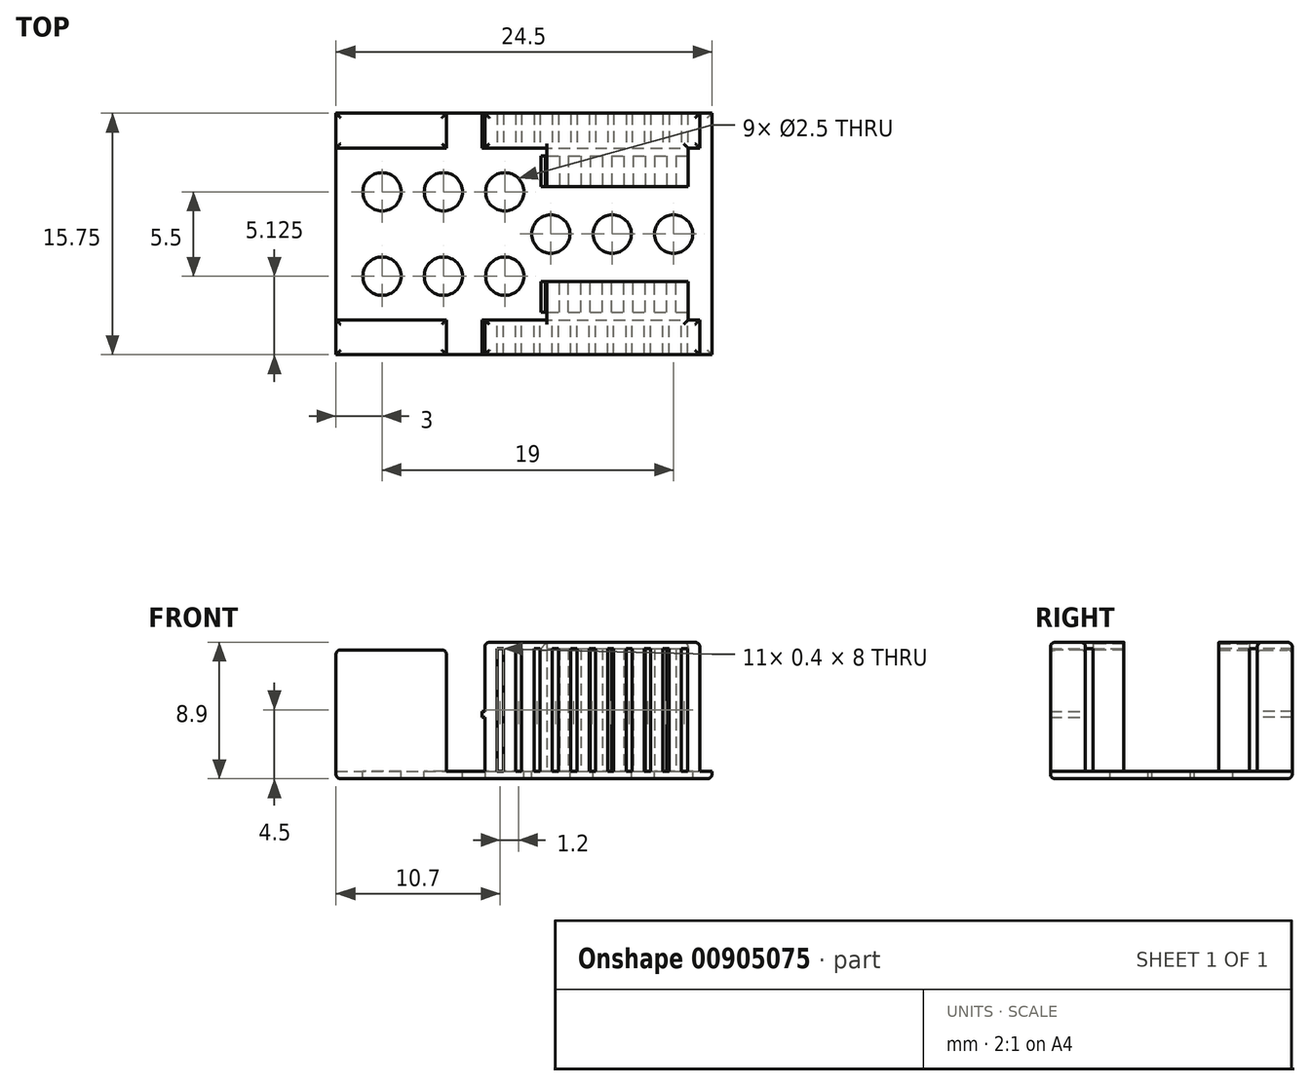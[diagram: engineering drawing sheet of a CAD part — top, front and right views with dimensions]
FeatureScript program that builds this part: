
annotation { "Feature Type Name" : "Feature", "Feature Type Description" : "" }
export const myFeature = defineFeature(function(context is Context, id is Id, definition is map)
    precondition{}
    {
        {
            var Q0;
            Q0=qCreatedBy(makeId("Top.planeOp"),FACE);
            var sketch = newSketch(context, id + "F0", { "sketchPlane" : qUnion([Q0])});
            skLineSegment(sketch, "E0.bottom", {"start": v(0, 0) * mm, "end": v(24.5, 0) * mm});
            skLineSegment(sketch, "E0.top", {"start": v(0, -15.75) * mm, "end": v(24.5, -15.75) * mm});
            skLineSegment(sketch, "E0.left", {"start": v(0, 0) * mm, "end": v(0, -15.75) * mm});
            skLineSegment(sketch, "E0.right", {"start": v(24.5, 0) * mm, "end": v(24.5, -15.75) * mm});
            skSolve(sketch);
        }
        {
            var Q0;
            Q0 = qSketchRegion(id + "F0", true);
            extrude(context, id + "F1", {"entities" : qUnion([Q0]), "depth" : .5 * mm, "offsetDistance" : 25 * mm});
        }
        {
            var Q0;
            Q0=makeQuery(id+"F1.opExtrude","CAP_FACE",FACE,{"disambiguationData":[OSD([sQuery(id+"F0.wireOp",EDGE,"E0.bottom"),sQuery(id+"F0.wireOp",EDGE,"E0.top"),sQuery(id+"F0.wireOp",EDGE,"E0.left"),sQuery(id+"F0.wireOp",EDGE,"E0.right")])],"isStart":false});
            var sketch = newSketch(context, id + "F2", { "sketchPlane" : qUnion([Q0])});
            skLineSegment(sketch, "E1", {"start": v(0, -2.28) * mm, "end": v(24.5, -2.27) * mm, "construction": true});
            skPoint(sketch, "E2", {"position": v(0, -7.87) * mm});
            skLineSegment(sketch, "E3", {"start": v(0, -7.87) * mm, "end": v(24.5, -7.87) * mm, "construction": true});
            skLineSegment(sketch, "E4.bottom", {"start": v(0, -2.28) * mm, "end": v(7.2, -2.28) * mm});
            skLineSegment(sketch, "E4.top", {"start": v(0, 0) * mm, "end": v(7.2, 0) * mm});
            skLineSegment(sketch, "E4.left", {"start": v(0, -2.28) * mm, "end": v(0, 0) * mm});
            skLineSegment(sketch, "E4.right", {"start": v(7.2, -2.28) * mm, "end": v(7.2, 0) * mm});
            skLineSegment(sketch, "E5.MirrorCS", {"start": v(0, -15.75) * mm, "end": v(7.2, -15.75) * mm});
            skLineSegment(sketch, "E6.MirrorCS", {"start": v(7.2, -13.47) * mm, "end": v(7.2, -15.75) * mm});
            skLineSegment(sketch, "E7.MirrorCS", {"start": v(0, -13.47) * mm, "end": v(0, -15.75) * mm});
            skLineSegment(sketch, "E8.MirrorCS", {"start": v(0, -13.47) * mm, "end": v(7.2, -13.47) * mm});
            skSolve(sketch);
        }
        {
            var Q0;
            Q0 = qSketchRegion(id + "F2", true);
            extrude(context, id + "F3", {"entities" : qUnion([Q0]), "operationType" : NewBodyOperationType.ADD, "depth" : 7.9 * mm, "offsetDistance" : 25 * mm});
        }
        {
            var Q0;
            Q0=makeQuery(id+"F1.opExtrude","CAP_FACE",FACE,{"disambiguationData":[OSD([sQuery(id+"F0.wireOp",EDGE,"E0.bottom"),sQuery(id+"F0.wireOp",EDGE,"E0.top"),sQuery(id+"F0.wireOp",EDGE,"E0.left"),sQuery(id+"F0.wireOp",EDGE,"E0.right")])],"isStart":false});
            var sketch = newSketch(context, id + "F4", { "sketchPlane" : qUnion([Q0])});
            skLineSegment(sketch, "E9", {"start": v(0, -7.88) * mm, "end": v(24.5, -7.87) * mm, "construction": true});
            skLineSegment(sketch, "E10.bottom", {"start": v(9.7, 0) * mm, "end": v(10.5, 0) * mm});
            skLineSegment(sketch, "E10.top", {"start": v(9.7, -2.28) * mm, "end": v(10.5, -2.28) * mm});
            skLineSegment(sketch, "E10.left", {"start": v(9.7, 0) * mm, "end": v(9.7, -2.28) * mm});
            skLineSegment(sketch, "E10.right", {"start": v(10.5, 0) * mm, "end": v(10.5, -2.28) * mm});
            skLineSegment(sketch, "E11.1.0.0", {"start": v(10.9, 0) * mm, "end": v(10.9, -2.28) * mm});
            skLineSegment(sketch, "E11.1.0.1", {"start": v(10.9, 0) * mm, "end": v(11.7, 0) * mm});
            skLineSegment(sketch, "E11.1.0.2", {"start": v(11.7, 0) * mm, "end": v(11.7, -2.28) * mm});
            skLineSegment(sketch, "E11.1.0.3", {"start": v(10.9, -2.28) * mm, "end": v(11.7, -2.28) * mm});
            skLineSegment(sketch, "E11.2.0.0", {"start": v(12.1, 0) * mm, "end": v(12.1, -2.28) * mm});
            skLineSegment(sketch, "E11.2.0.1", {"start": v(12.1, 0) * mm, "end": v(12.9, 0) * mm});
            skLineSegment(sketch, "E11.2.0.2", {"start": v(12.9, 0) * mm, "end": v(12.9, -2.28) * mm});
            skLineSegment(sketch, "E11.2.0.3", {"start": v(12.1, -2.28) * mm, "end": v(12.9, -2.28) * mm});
            skLineSegment(sketch, "E11.3.0.0", {"start": v(13.3, 0) * mm, "end": v(13.3, -2.28) * mm});
            skLineSegment(sketch, "E11.3.0.1", {"start": v(13.3, 0) * mm, "end": v(14.1, 0) * mm});
            skLineSegment(sketch, "E11.3.0.2", {"start": v(14.1, 0) * mm, "end": v(14.1, -2.28) * mm});
            skLineSegment(sketch, "E11.3.0.3", {"start": v(13.3, -2.28) * mm, "end": v(14.1, -2.28) * mm});
            skLineSegment(sketch, "E11.4.0.0", {"start": v(14.5, 0) * mm, "end": v(14.5, -2.28) * mm});
            skLineSegment(sketch, "E11.4.0.1", {"start": v(14.5, 0) * mm, "end": v(15.3, 0) * mm});
            skLineSegment(sketch, "E11.4.0.2", {"start": v(15.3, 0) * mm, "end": v(15.3, -2.28) * mm});
            skLineSegment(sketch, "E11.4.0.3", {"start": v(14.5, -2.28) * mm, "end": v(15.3, -2.28) * mm});
            skLineSegment(sketch, "E11.direction1", {"start": v(9.7, -2.28) * mm, "end": v(10.9, -2.28) * mm, "construction": true});
            skLineSegment(sketch, "E12.MirrorCS", {"start": v(9.7, -13.48) * mm, "end": v(10.5, -13.48) * mm});
            skLineSegment(sketch, "E13.MirrorCS", {"start": v(10.9, -15.75) * mm, "end": v(11.7, -15.75) * mm});
            skLineSegment(sketch, "E14.MirrorCS", {"start": v(14.5, -15.75) * mm, "end": v(14.5, -13.48) * mm});
            skLineSegment(sketch, "E15.MirrorCS", {"start": v(14.5, -15.75) * mm, "end": v(15.3, -15.75) * mm});
            skLineSegment(sketch, "E16.MirrorCS", {"start": v(12.1, -13.48) * mm, "end": v(12.9, -13.48) * mm});
            skLineSegment(sketch, "E17.MirrorCS", {"start": v(15.3, -15.75) * mm, "end": v(15.3, -13.48) * mm});
            skLineSegment(sketch, "E18.MirrorCS", {"start": v(10.9, -15.75) * mm, "end": v(10.9, -13.48) * mm});
            skLineSegment(sketch, "E19.MirrorCS", {"start": v(12.9, -15.75) * mm, "end": v(12.9, -13.48) * mm});
            skLineSegment(sketch, "E20.MirrorCS", {"start": v(13.3, -15.75) * mm, "end": v(14.1, -15.75) * mm});
            skLineSegment(sketch, "E21.MirrorCS", {"start": v(14.5, -13.48) * mm, "end": v(15.3, -13.48) * mm});
            skLineSegment(sketch, "E22.MirrorCS", {"start": v(10.5, -15.75) * mm, "end": v(10.5, -13.48) * mm});
            skLineSegment(sketch, "E23.MirrorCS", {"start": v(12.1, -15.75) * mm, "end": v(12.9, -15.75) * mm});
            skLineSegment(sketch, "E24.MirrorCS", {"start": v(9.7, -13.48) * mm, "end": v(10.9, -13.48) * mm, "construction": true});
            skLineSegment(sketch, "E25.MirrorCS", {"start": v(13.3, -15.75) * mm, "end": v(13.3, -13.48) * mm});
            skLineSegment(sketch, "E26.MirrorCS", {"start": v(9.7, -15.75) * mm, "end": v(9.7, -13.48) * mm});
            skLineSegment(sketch, "E27.MirrorCS", {"start": v(12.1, -15.75) * mm, "end": v(12.1, -13.48) * mm});
            skLineSegment(sketch, "E28.MirrorCS", {"start": v(14.1, -15.75) * mm, "end": v(14.1, -13.48) * mm});
            skLineSegment(sketch, "E29.MirrorCS", {"start": v(13.3, -13.48) * mm, "end": v(14.1, -13.48) * mm});
            skLineSegment(sketch, "E30.MirrorCS", {"start": v(9.7, -15.75) * mm, "end": v(10.5, -15.75) * mm});
            skLineSegment(sketch, "E31.MirrorCS", {"start": v(10.9, -13.48) * mm, "end": v(11.7, -13.48) * mm});
            skLineSegment(sketch, "E32.MirrorCS", {"start": v(11.7, -15.75) * mm, "end": v(11.7, -13.48) * mm});
            skLineSegment(sketch, "E33.0.5.0", {"start": v(15.7, 0) * mm, "end": v(15.7, -2.28) * mm});
            skLineSegment(sketch, "E33.3.5.0", {"start": v(15.7, 0) * mm, "end": v(16.5, 0) * mm});
            skLineSegment(sketch, "E33.6.5.0", {"start": v(16.5, 0) * mm, "end": v(16.5, -2.28) * mm});
            skLineSegment(sketch, "E33.9.5.0", {"start": v(15.7, -2.28) * mm, "end": v(16.5, -2.28) * mm});
            skLineSegment(sketch, "E33.0.6.0", {"start": v(16.9, 0) * mm, "end": v(16.9, -2.28) * mm});
            skLineSegment(sketch, "E33.3.6.0", {"start": v(16.9, 0) * mm, "end": v(17.7, 0) * mm});
            skLineSegment(sketch, "E33.6.6.0", {"start": v(17.7, 0) * mm, "end": v(17.7, -2.28) * mm});
            skLineSegment(sketch, "E33.9.6.0", {"start": v(16.9, -2.28) * mm, "end": v(17.7, -2.28) * mm});
            skLineSegment(sketch, "E33.0.7.0", {"start": v(18.1, 0) * mm, "end": v(18.1, -2.28) * mm});
            skLineSegment(sketch, "E33.3.7.0", {"start": v(18.1, 0) * mm, "end": v(18.9, 0) * mm});
            skLineSegment(sketch, "E33.6.7.0", {"start": v(18.9, 0) * mm, "end": v(18.9, -2.28) * mm});
            skLineSegment(sketch, "E33.9.7.0", {"start": v(18.1, -2.28) * mm, "end": v(18.9, -2.28) * mm});
            skLineSegment(sketch, "E34.MirrorCS", {"start": v(18.9, -15.75) * mm, "end": v(18.9, -13.47) * mm});
            skLineSegment(sketch, "E35.MirrorCS", {"start": v(16.5, -15.75) * mm, "end": v(16.5, -13.48) * mm});
            skLineSegment(sketch, "E36.MirrorCS", {"start": v(15.7, -13.48) * mm, "end": v(16.5, -13.48) * mm});
            skLineSegment(sketch, "E37.MirrorCS", {"start": v(15.7, -15.75) * mm, "end": v(15.7, -13.48) * mm});
            skLineSegment(sketch, "E38.MirrorCS", {"start": v(16.9, -15.75) * mm, "end": v(16.9, -13.48) * mm});
            skLineSegment(sketch, "E39.MirrorCS", {"start": v(18.1, -15.75) * mm, "end": v(18.1, -13.47) * mm});
            skLineSegment(sketch, "E40.MirrorCS", {"start": v(18.1, -15.75) * mm, "end": v(18.9, -15.75) * mm});
            skLineSegment(sketch, "E41.MirrorCS", {"start": v(15.7, -15.75) * mm, "end": v(16.5, -15.75) * mm});
            skLineSegment(sketch, "E42.MirrorCS", {"start": v(17.7, -15.75) * mm, "end": v(17.7, -13.48) * mm});
            skLineSegment(sketch, "E43.MirrorCS", {"start": v(16.9, -15.75) * mm, "end": v(17.7, -15.75) * mm});
            skLineSegment(sketch, "E44.MirrorCS", {"start": v(16.9, -13.48) * mm, "end": v(17.7, -13.48) * mm});
            skLineSegment(sketch, "E45.MirrorCS", {"start": v(18.1, -13.47) * mm, "end": v(18.9, -13.47) * mm});
            skLineSegment(sketch, "E46.0.8.0", {"start": v(19.3, 0) * mm, "end": v(19.3, -2.28) * mm});
            skLineSegment(sketch, "E46.3.8.0", {"start": v(19.3, 0) * mm, "end": v(20.1, 0) * mm});
            skLineSegment(sketch, "E46.6.8.0", {"start": v(20.1, 0) * mm, "end": v(20.1, -2.28) * mm});
            skLineSegment(sketch, "E46.9.8.0", {"start": v(19.3, -2.28) * mm, "end": v(20.1, -2.28) * mm});
            skLineSegment(sketch, "E46.0.9.0", {"start": v(20.5, 0) * mm, "end": v(20.5, -2.28) * mm});
            skLineSegment(sketch, "E46.3.9.0", {"start": v(20.5, 0) * mm, "end": v(21.3, 0) * mm});
            skLineSegment(sketch, "E46.6.9.0", {"start": v(21.3, 0) * mm, "end": v(21.3, -2.28) * mm});
            skLineSegment(sketch, "E46.9.9.0", {"start": v(20.5, -2.28) * mm, "end": v(21.3, -2.28) * mm});
            skLineSegment(sketch, "E46.0.10.0", {"start": v(21.7, 0) * mm, "end": v(21.7, -2.28) * mm});
            skLineSegment(sketch, "E46.3.10.0", {"start": v(21.7, 0) * mm, "end": v(22.5, 0) * mm});
            skLineSegment(sketch, "E46.6.10.0", {"start": v(22.5, 0) * mm, "end": v(22.5, -2.28) * mm});
            skLineSegment(sketch, "E46.9.10.0", {"start": v(21.7, -2.28) * mm, "end": v(22.5, -2.28) * mm});
            skLineSegment(sketch, "E46.0.11.0", {"start": v(22.9, 0) * mm, "end": v(22.9, -2.28) * mm});
            skLineSegment(sketch, "E46.3.11.0", {"start": v(22.9, 0) * mm, "end": v(23.7, 0) * mm});
            skLineSegment(sketch, "E46.6.11.0", {"start": v(23.7, 0) * mm, "end": v(23.7, -2.28) * mm});
            skLineSegment(sketch, "E46.9.11.0", {"start": v(22.9, -2.28) * mm, "end": v(23.7, -2.28) * mm});
            skLineSegment(sketch, "E47.MirrorCS", {"start": v(19.3, -13.47) * mm, "end": v(20.1, -13.47) * mm});
            skLineSegment(sketch, "E48.MirrorCS", {"start": v(19.3, -15.75) * mm, "end": v(19.3, -13.47) * mm});
            skLineSegment(sketch, "E49.MirrorCS", {"start": v(20.1, -15.75) * mm, "end": v(20.1, -13.47) * mm});
            skLineSegment(sketch, "E50.MirrorCS", {"start": v(19.3, -15.75) * mm, "end": v(20.1, -15.75) * mm});
            skLineSegment(sketch, "E51.MirrorCS", {"start": v(20.5, -15.75) * mm, "end": v(20.5, -13.47) * mm});
            skLineSegment(sketch, "E52.MirrorCS", {"start": v(20.5, -13.47) * mm, "end": v(21.3, -13.47) * mm});
            skLineSegment(sketch, "E53.MirrorCS", {"start": v(21.3, -15.75) * mm, "end": v(21.3, -13.47) * mm});
            skLineSegment(sketch, "E54.MirrorCS", {"start": v(20.5, -15.75) * mm, "end": v(21.3, -15.75) * mm});
            skLineSegment(sketch, "E55.MirrorCS", {"start": v(21.7, -15.75) * mm, "end": v(21.7, -13.47) * mm});
            skLineSegment(sketch, "E56.MirrorCS", {"start": v(21.7, -13.47) * mm, "end": v(22.5, -13.47) * mm});
            skLineSegment(sketch, "E57.MirrorCS", {"start": v(22.5, -15.75) * mm, "end": v(22.5, -13.47) * mm});
            skLineSegment(sketch, "E58.MirrorCS", {"start": v(21.7, -15.75) * mm, "end": v(22.5, -15.75) * mm});
            skLineSegment(sketch, "E59.MirrorCS", {"start": v(22.9, -15.75) * mm, "end": v(22.9, -13.47) * mm});
            skLineSegment(sketch, "E60.MirrorCS", {"start": v(22.9, -13.47) * mm, "end": v(23.7, -13.47) * mm});
            skLineSegment(sketch, "E61.MirrorCS", {"start": v(23.7, -15.75) * mm, "end": v(23.7, -13.47) * mm});
            skLineSegment(sketch, "E62.MirrorCS", {"start": v(22.9, -15.75) * mm, "end": v(23.7, -15.75) * mm});
            skSolve(sketch);
        }
        {
            var Q0;
            Q0 = qSketchRegion(id + "F4", true);
            extrude(context, id + "F5", {"entities" : qUnion([Q0]), "operationType" : NewBodyOperationType.ADD, "depth" : 8 * mm, "offsetDistance" : 25 * mm});
        }
        {
            var Q0;
            Q0=makeQuery(id+"F5.opExtrude","SWEPT_FACE",FACE,{"disambiguationData":[OSD([sQuery(id+"F4.wireOp",EDGE,"E10.left")])]});
            var sketch = newSketch(context, id + "F6", { "sketchPlane" : qUnion([Q0])});
            skLineSegment(sketch, "E63.bottom", {"start": v(0, 4) * mm, "end": v(2.27, 4) * mm});
            skLineSegment(sketch, "E63.top", {"start": v(0, 4.4) * mm, "end": v(2.28, 4.4) * mm});
            skLineSegment(sketch, "E63.left", {"start": v(0, 4) * mm, "end": v(0, 4.4) * mm});
            skLineSegment(sketch, "E63.right", {"start": v(2.28, 4) * mm, "end": v(2.28, 4.4) * mm});
            skLineSegment(sketch, "E64", {"start": v(7.88, 0) * mm, "end": v(7.88, 8.23) * mm, "construction": true});
            skLineSegment(sketch, "E65.MirrorCS", {"start": v(15.75, 4) * mm, "end": v(15.75, 4.4) * mm});
            skLineSegment(sketch, "E66.MirrorCS", {"start": v(13.47, 4) * mm, "end": v(13.47, 4.4) * mm});
            skLineSegment(sketch, "E67.MirrorCS", {"start": v(15.75, 4) * mm, "end": v(13.48, 4) * mm});
            skLineSegment(sketch, "E68.MirrorCS", {"start": v(15.75, 4.4) * mm, "end": v(13.47, 4.4) * mm});
            skSolve(sketch);
        }
        {
            var Q0;
            Q0 = qSketchRegion(id + "F6", true);
            extrude(context, id + "F7", {"entities" : qUnion([Q0]), "operationType" : NewBodyOperationType.ADD, "depth" : .2 * mm, "offsetDistance" : 25 * mm});
        }
        {
            var Q0;
            Q0=makeQuery(id+"F1.opExtrude","CAP_FACE",FACE,{"disambiguationData":[OSD([sQuery(id+"F0.wireOp",EDGE,"E0.bottom"),sQuery(id+"F0.wireOp",EDGE,"E0.top"),sQuery(id+"F0.wireOp",EDGE,"E0.left"),sQuery(id+"F0.wireOp",EDGE,"E0.right")])],"isStart":false});
            var sketch = newSketch(context, id + "F8", { "sketchPlane" : qUnion([Q0])});
            skLineSegment(sketch, "E69", {"start": v(13.75, 0) * mm, "end": v(13.75, -15.77) * mm, "construction": true});
            skLineSegment(sketch, "E70", {"start": v(24.5, -7.88) * mm, "end": v(0, -7.88) * mm, "construction": true});
            skLineSegment(sketch, "E71.bottom", {"start": v(13.75, -2.78) * mm, "end": v(14.55, -2.78) * mm});
            skLineSegment(sketch, "E71.top", {"start": v(13.75, -4.78) * mm, "end": v(14.55, -4.78) * mm});
            skLineSegment(sketch, "E71.left", {"start": v(13.75, -2.78) * mm, "end": v(13.75, -4.78) * mm});
            skLineSegment(sketch, "E71.right", {"start": v(14.55, -2.78) * mm, "end": v(14.55, -4.78) * mm});
            skLineSegment(sketch, "E72.direction1", {"start": v(13.75, -4.78) * mm, "end": v(15.15, -4.78) * mm, "construction": true});
            skLineSegment(sketch, "E72.direction2", {"start": v(13.75, -4.78) * mm, "end": v(13.75, -7.28) * mm, "construction": true});
            skLineSegment(sketch, "E73.0.1.0", {"start": v(15.15, -2.78) * mm, "end": v(15.15, -4.78) * mm});
            skLineSegment(sketch, "E73.3.1.0", {"start": v(15.15, -2.78) * mm, "end": v(15.95, -2.78) * mm});
            skLineSegment(sketch, "E73.6.1.0", {"start": v(15.15, -4.78) * mm, "end": v(15.95, -4.78) * mm});
            skLineSegment(sketch, "E73.9.1.0", {"start": v(15.95, -2.78) * mm, "end": v(15.95, -4.78) * mm});
            skLineSegment(sketch, "E74.MirrorCS", {"start": v(13.75, -10.98) * mm, "end": v(14.55, -10.98) * mm});
            skLineSegment(sketch, "E75.MirrorCS", {"start": v(15.15, -10.98) * mm, "end": v(15.95, -10.97) * mm});
            skLineSegment(sketch, "E76.MirrorCS", {"start": v(13.75, -12.98) * mm, "end": v(13.75, -10.98) * mm});
            skLineSegment(sketch, "E77.MirrorCS", {"start": v(14.55, -12.98) * mm, "end": v(14.55, -10.98) * mm});
            skLineSegment(sketch, "E78.MirrorCS", {"start": v(13.75, -12.98) * mm, "end": v(14.55, -12.98) * mm});
            skLineSegment(sketch, "E79.MirrorCS", {"start": v(15.15, -12.98) * mm, "end": v(15.95, -12.98) * mm});
            skLineSegment(sketch, "E80.MirrorCS", {"start": v(15.95, -12.97) * mm, "end": v(15.95, -10.98) * mm});
            skLineSegment(sketch, "E81.MirrorCS", {"start": v(15.15, -12.97) * mm, "end": v(15.15, -10.98) * mm});
            skLineSegment(sketch, "E82.MirrorCS", {"start": v(13.75, -10.98) * mm, "end": v(15.15, -10.98) * mm, "construction": true});
            skLineSegment(sketch, "E83.MirrorCS", {"start": v(13.75, -10.98) * mm, "end": v(13.75, -8.48) * mm, "construction": true});
            skLineSegment(sketch, "E84.0.2.0", {"start": v(16.55, -2.78) * mm, "end": v(16.55, -4.78) * mm});
            skLineSegment(sketch, "E84.3.2.0", {"start": v(16.55, -2.78) * mm, "end": v(17.35, -2.78) * mm});
            skLineSegment(sketch, "E84.6.2.0", {"start": v(16.55, -4.78) * mm, "end": v(17.35, -4.78) * mm});
            skLineSegment(sketch, "E84.9.2.0", {"start": v(17.35, -2.78) * mm, "end": v(17.35, -4.78) * mm});
            skLineSegment(sketch, "E85.MirrorCS", {"start": v(16.55, -10.98) * mm, "end": v(17.35, -10.98) * mm});
            skLineSegment(sketch, "E86.MirrorCS", {"start": v(16.55, -12.97) * mm, "end": v(17.35, -12.97) * mm});
            skLineSegment(sketch, "E87.MirrorCS", {"start": v(17.35, -12.97) * mm, "end": v(17.35, -10.98) * mm});
            skLineSegment(sketch, "E88.MirrorCS", {"start": v(16.55, -12.97) * mm, "end": v(16.55, -10.98) * mm});
            skLineSegment(sketch, "E89.0.3.0", {"start": v(17.95, -2.78) * mm, "end": v(17.95, -4.78) * mm});
            skLineSegment(sketch, "E89.3.3.0", {"start": v(17.95, -2.78) * mm, "end": v(18.75, -2.78) * mm});
            skLineSegment(sketch, "E89.6.3.0", {"start": v(17.95, -4.78) * mm, "end": v(18.75, -4.78) * mm});
            skLineSegment(sketch, "E89.9.3.0", {"start": v(18.75, -2.78) * mm, "end": v(18.75, -4.78) * mm});
            skLineSegment(sketch, "E89.0.4.0", {"start": v(19.35, -2.78) * mm, "end": v(19.35, -4.78) * mm});
            skLineSegment(sketch, "E89.3.4.0", {"start": v(19.35, -2.78) * mm, "end": v(20.15, -2.78) * mm});
            skLineSegment(sketch, "E89.6.4.0", {"start": v(19.35, -4.78) * mm, "end": v(20.15, -4.78) * mm});
            skLineSegment(sketch, "E89.9.4.0", {"start": v(20.15, -2.78) * mm, "end": v(20.15, -4.78) * mm});
            skLineSegment(sketch, "E89.0.5.0", {"start": v(20.75, -2.78) * mm, "end": v(20.75, -4.78) * mm});
            skLineSegment(sketch, "E89.3.5.0", {"start": v(20.75, -2.78) * mm, "end": v(21.55, -2.78) * mm});
            skLineSegment(sketch, "E89.6.5.0", {"start": v(20.75, -4.78) * mm, "end": v(21.55, -4.78) * mm});
            skLineSegment(sketch, "E89.9.5.0", {"start": v(21.55, -2.78) * mm, "end": v(21.55, -4.78) * mm});
            skLineSegment(sketch, "E89.0.6.0", {"start": v(22.15, -2.78) * mm, "end": v(22.15, -4.78) * mm});
            skLineSegment(sketch, "E89.3.6.0", {"start": v(22.15, -2.78) * mm, "end": v(22.95, -2.78) * mm});
            skLineSegment(sketch, "E89.6.6.0", {"start": v(22.15, -4.78) * mm, "end": v(22.95, -4.78) * mm});
            skLineSegment(sketch, "E89.9.6.0", {"start": v(22.95, -2.78) * mm, "end": v(22.95, -4.78) * mm});
            skLineSegment(sketch, "E90.MirrorCS", {"start": v(18.75, -12.97) * mm, "end": v(18.75, -10.97) * mm});
            skLineSegment(sketch, "E91.MirrorCS", {"start": v(20.75, -12.97) * mm, "end": v(20.75, -10.97) * mm});
            skLineSegment(sketch, "E92.MirrorCS", {"start": v(21.55, -12.97) * mm, "end": v(21.55, -10.97) * mm});
            skLineSegment(sketch, "E93.MirrorCS", {"start": v(17.95, -10.98) * mm, "end": v(18.75, -10.98) * mm});
            skLineSegment(sketch, "E94.MirrorCS", {"start": v(22.15, -12.97) * mm, "end": v(22.15, -10.97) * mm});
            skLineSegment(sketch, "E95.MirrorCS", {"start": v(20.75, -10.97) * mm, "end": v(21.55, -10.97) * mm});
            skLineSegment(sketch, "E96.MirrorCS", {"start": v(19.35, -12.97) * mm, "end": v(19.35, -10.97) * mm});
            skLineSegment(sketch, "E97.MirrorCS", {"start": v(22.15, -12.97) * mm, "end": v(22.95, -12.97) * mm});
            skLineSegment(sketch, "E98.MirrorCS", {"start": v(20.75, -12.97) * mm, "end": v(21.55, -12.97) * mm});
            skLineSegment(sketch, "E99.MirrorCS", {"start": v(22.15, -10.97) * mm, "end": v(22.95, -10.97) * mm});
            skLineSegment(sketch, "E100.MirrorCS", {"start": v(17.95, -12.97) * mm, "end": v(17.95, -10.98) * mm});
            skLineSegment(sketch, "E101.MirrorCS", {"start": v(22.95, -12.97) * mm, "end": v(22.95, -10.97) * mm});
            skLineSegment(sketch, "E102.MirrorCS", {"start": v(19.35, -10.97) * mm, "end": v(20.15, -10.97) * mm});
            skLineSegment(sketch, "E103.MirrorCS", {"start": v(20.15, -12.97) * mm, "end": v(20.15, -10.97) * mm});
            skLineSegment(sketch, "E104.MirrorCS", {"start": v(17.95, -12.97) * mm, "end": v(18.75, -12.97) * mm});
            skLineSegment(sketch, "E105.MirrorCS", {"start": v(19.35, -12.97) * mm, "end": v(20.15, -12.97) * mm});
            skSolve(sketch);
        }
        {
            var Q0;
            Q0 = qSketchRegion(id + "F8", true);
            extrude(context, id + "F9", {"entities" : qUnion([Q0]), "operationType" : NewBodyOperationType.ADD, "depth" : 8 * mm, "offsetDistance" : 25 * mm});
        }
        {
            var Q0;
            Q0=makeQuery(id+"F5.opExtrude","CAP_FACE",FACE,{"disambiguationData":[OSD([sQuery(id+"F4.wireOp",EDGE,"E10.bottom"),sQuery(id+"F4.wireOp",EDGE,"E10.top"),sQuery(id+"F4.wireOp",EDGE,"E10.left"),sQuery(id+"F4.wireOp",EDGE,"E10.right")])],"isStart":false});
            var sketch = newSketch(context, id + "F10", { "sketchPlane" : qUnion([Q0])});
            skLineSegment(sketch, "E106.bottom", {"start": v(9.7, 0) * mm, "end": v(23.7, 0) * mm});
            skLineSegment(sketch, "E106.top", {"start": v(9.7, -2.28) * mm, "end": v(23.7, -2.28) * mm});
            skLineSegment(sketch, "E106.left", {"start": v(9.7, 0) * mm, "end": v(9.7, -2.28) * mm});
            skLineSegment(sketch, "E106.right", {"start": v(23.7, 0) * mm, "end": v(23.7, -2.28) * mm});
            skLineSegment(sketch, "E107.bottom", {"start": v(13.75, -4.78) * mm, "end": v(22.95, -4.78) * mm});
            skLineSegment(sketch, "E107.top", {"start": v(13.75, -2.28) * mm, "end": v(22.95, -2.28) * mm});
            skLineSegment(sketch, "E107.left", {"start": v(13.75, -4.78) * mm, "end": v(13.75, -2.28) * mm});
            skLineSegment(sketch, "E107.right", {"start": v(22.95, -4.78) * mm, "end": v(22.95, -2.28) * mm});
            skLineSegment(sketch, "E108", {"start": v(24.5, -7.88) * mm, "end": v(6.87, -7.88) * mm, "construction": true});
            skLineSegment(sketch, "E109.MirrorCS", {"start": v(13.75, -13.47) * mm, "end": v(22.95, -13.47) * mm});
            skLineSegment(sketch, "E110.MirrorCS", {"start": v(13.75, -10.98) * mm, "end": v(13.75, -13.47) * mm});
            skLineSegment(sketch, "E111.MirrorCS", {"start": v(23.7, -15.75) * mm, "end": v(23.7, -13.47) * mm});
            skLineSegment(sketch, "E112.MirrorCS", {"start": v(13.75, -10.98) * mm, "end": v(22.95, -10.97) * mm});
            skLineSegment(sketch, "E113.MirrorCS", {"start": v(9.7, -15.75) * mm, "end": v(23.7, -15.75) * mm});
            skLineSegment(sketch, "E114.MirrorCS", {"start": v(22.95, -10.97) * mm, "end": v(22.95, -13.47) * mm});
            skLineSegment(sketch, "E115.MirrorCS", {"start": v(9.7, -15.75) * mm, "end": v(9.7, -13.47) * mm});
            skLineSegment(sketch, "E116.MirrorCS", {"start": v(9.7, -13.48) * mm, "end": v(23.7, -13.47) * mm});
            skSolve(sketch);
        }
        {
            var Q0;
            Q0 = qSketchRegion(id + "F10", true);
            extrude(context, id + "F11", {"entities" : qUnion([Q0]), "operationType" : NewBodyOperationType.ADD, "depth" : .4 * mm, "offsetDistance" : 25 * mm});
        }
        {
            var Q0;
            Q0=makeQuery(id+"F11.boolean.opBoolean","MERGE",FACE,{"derivedFrom":[makeQuery(id+"F9.opExtrude","SWEPT_FACE",FACE,{"disambiguationData":[OSD([sQuery(id+"F8.wireOp",EDGE,"E71.left")])]}),makeQuery(id+"F11.opExtrude","SWEPT_FACE",FACE,{"disambiguationData":[OSD([sQuery(id+"F10.wireOp",EDGE,"E107.left")])]})]});
            var sketch = newSketch(context, id + "F12", { "sketchPlane" : qUnion([Q0])});
            skLineSegment(sketch, "E117.bottom", {"start": v(4.78, 8.8) * mm, "end": v(2.78, 8.8) * mm});
            skLineSegment(sketch, "E117.top", {"start": v(4.78, 8.4) * mm, "end": v(2.78, 8.4) * mm});
            skLineSegment(sketch, "E117.left", {"start": v(4.78, 8.8) * mm, "end": v(4.78, 8.4) * mm});
            skLineSegment(sketch, "E117.right", {"start": v(2.78, 8.8) * mm, "end": v(2.78, 8.4) * mm});
            skLineSegment(sketch, "E118", {"start": v(7.88, 0) * mm, "end": v(7.88, 9.2) * mm, "construction": true});
            skLineSegment(sketch, "E119.MirrorCS", {"start": v(10.97, 8.8) * mm, "end": v(10.97, 8.4) * mm});
            skLineSegment(sketch, "E120.MirrorCS", {"start": v(10.97, 8.8) * mm, "end": v(12.97, 8.8) * mm});
            skLineSegment(sketch, "E121.MirrorCS", {"start": v(10.97, 8.4) * mm, "end": v(12.97, 8.4) * mm});
            skLineSegment(sketch, "E122.MirrorCS", {"start": v(12.97, 8.8) * mm, "end": v(12.97, 8.4) * mm});
            skSolve(sketch);
        }
        {
            var Q0;
            Q0 = qSketchRegion(id + "F12", true);
            extrude(context, id + "F13", {"entities" : qUnion([Q0]), "operationType" : NewBodyOperationType.ADD, "depth" : .4 * mm, "offsetDistance" : 25 * mm});
        }
        {
            var Q0;
            Q0=makeQuery(id+"F13.opExtrude","CAP_EDGE",EDGE,{"disambiguationData":[OSD([sQuery(id+"F12.wireOp",EDGE,"E117.bottom")])],"isStart":false});
            var Q1;
            Q1=makeQuery(id+"F13.opExtrude","CAP_EDGE",EDGE,{"disambiguationData":[OSD([sQuery(id+"F12.wireOp",EDGE,"E120.MirrorCS")])],"isStart":false});
            chamfer(context, id + "F14", {"entities" : qUnion([Q0, Q1]), "width" : .3 * mm, "tangentPropagation" : true});
        }
        {
            var Q0;
            Q0=makeQuery(id+"F1.opExtrude","CAP_EDGE",EDGE,{"disambiguationData":[OSD([sQuery(id+"F0.wireOp",EDGE,"E0.bottom")])],"isStart":true});
            var Q1;
            Q1=makeQuery(id+"F1.opExtrude","CAP_EDGE",EDGE,{"disambiguationData":[OSD([sQuery(id+"F0.wireOp",EDGE,"E0.left")])],"isStart":true});
            var Q2;
            Q2=makeQuery(id+"F1.opExtrude","CAP_EDGE",EDGE,{"disambiguationData":[OSD([sQuery(id+"F0.wireOp",EDGE,"E0.top")])],"isStart":true});
            var Q3;
            Q3=makeQuery(id+"F1.opExtrude","CAP_EDGE",EDGE,{"disambiguationData":[OSD([sQuery(id+"F0.wireOp",EDGE,"E0.right")])],"isStart":true});
            var Q4;
            Q4=makeQuery(id+"F3.opExtrude","CAP_EDGE",EDGE,{"disambiguationData":[OSD([sQuery(id+"F2.wireOp",EDGE,"E7.MirrorCS")])],"isStart":false});
            var Q5;
            Q5=makeQuery(id+"F3.opExtrude","CAP_EDGE",EDGE,{"disambiguationData":[OSD([sQuery(id+"F2.wireOp",EDGE,"E8.MirrorCS")])],"isStart":false});
            var Q6;
            Q6=makeQuery(id+"F3.opExtrude","CAP_FACE",FACE,{"disambiguationData":[OSD([sQuery(id+"F2.wireOp",EDGE,"E5.MirrorCS"),sQuery(id+"F2.wireOp",EDGE,"E6.MirrorCS"),sQuery(id+"F2.wireOp",EDGE,"E7.MirrorCS"),sQuery(id+"F2.wireOp",EDGE,"E8.MirrorCS")])],"isStart":false});
            var Q7;
            Q7=makeQuery(id+"F3.opExtrude","CAP_EDGE",EDGE,{"disambiguationData":[OSD([sQuery(id+"F2.wireOp",EDGE,"E4.bottom")])],"isStart":false});
            var Q8;
            Q8=makeQuery(id+"F3.opExtrude","CAP_EDGE",EDGE,{"disambiguationData":[OSD([sQuery(id+"F2.wireOp",EDGE,"E4.left")])],"isStart":false});
            var Q9;
            Q9=makeQuery(id+"F3.opExtrude","CAP_FACE",FACE,{"disambiguationData":[OSD([sQuery(id+"F2.wireOp",EDGE,"E4.bottom"),sQuery(id+"F2.wireOp",EDGE,"E4.top"),sQuery(id+"F2.wireOp",EDGE,"E4.left"),sQuery(id+"F2.wireOp",EDGE,"E4.right")])],"isStart":false});
            var Q10;
            {var subQ0=sQuery(id+"F10.wireOp",EDGE,"E106.top");var subQ1=makeQuery(id+"F10.imprint","INTERSECT",VERTEX,{"derivedFrom":[makeQuery(id+"F5.opExtrude","CAP_EDGE",EDGE,{"disambiguationData":[OSD([sQuery(id+"F4.wireOp",EDGE,"E10.right")])],"isStart":false}),subQ0]});Q10=makeQuery(id+"F11.opExtrude","CAP_EDGE",EDGE,{"disambiguationData":[OSD([subQ0]),TDD([makeQuery(id+"F10.imprint","IMPRINT",EDGE,{"disambiguationData":[TD([[subQ1,-1.0]])],"derivedFrom":subQ0}),makeQuery(id+"F10.imprint","IMPRINT",EDGE,{"disambiguationData":[TD([[makeQuery(id+"F10.imprint","INTERSECT",VERTEX,{"derivedFrom":[subQ0,sQuery(id+"F10.wireOp",EDGE,"E106.left")]}),-1.0]])],"derivedFrom":subQ0})])],"isStart":false});}
            var Q11;
            Q11=makeQuery(id+"F11.opExtrude","CAP_EDGE",EDGE,{"disambiguationData":[OSD([sQuery(id+"F10.wireOp",EDGE,"E106.left")])],"isStart":false});
            var Q12;
            Q12=makeQuery(id+"F11.opExtrude","CAP_EDGE",EDGE,{"disambiguationData":[OSD([sQuery(id+"F10.wireOp",EDGE,"E106.bottom")])],"isStart":false});
            var Q13;
            Q13=makeQuery(id+"F11.opExtrude","CAP_EDGE",EDGE,{"disambiguationData":[OSD([sQuery(id+"F10.wireOp",EDGE,"E106.right")])],"isStart":false});
            var Q14;
            {var subQ0=sQuery(id+"F10.wireOp",EDGE,"E106.top");Q14=makeQuery(id+"F11.opExtrude","CAP_EDGE",EDGE,{"disambiguationData":[OSD([subQ0]),TDD([makeQuery(id+"F10.imprint","IMPRINT",EDGE,{"disambiguationData":[TD([[makeQuery(id+"F10.imprint","INTERSECT",VERTEX,{"derivedFrom":[subQ0,sQuery(id+"F10.wireOp",EDGE,"E106.right")]}),1.0]])],"derivedFrom":subQ0})])],"isStart":false});}
            var Q15;
            Q15=makeQuery(id+"F11.opExtrude","CAP_EDGE",EDGE,{"disambiguationData":[OSD([sQuery(id+"F10.wireOp",EDGE,"E107.right")])],"isStart":false});
            var Q16;
            Q16=makeQuery(id+"F11.opExtrude","CAP_EDGE",EDGE,{"disambiguationData":[OSD([sQuery(id+"F10.wireOp",EDGE,"E114.MirrorCS")])],"isStart":false});
            var Q17;
            {var subQ0=sQuery(id+"F10.wireOp",EDGE,"E116.MirrorCS");Q17=makeQuery(id+"F11.opExtrude","CAP_EDGE",EDGE,{"disambiguationData":[OSD([subQ0]),TDD([makeQuery(id+"F10.imprint","IMPRINT",EDGE,{"disambiguationData":[TD([[makeQuery(id+"F10.imprint","INTERSECT",VERTEX,{"derivedFrom":[sQuery(id+"F10.wireOp",EDGE,"E111.MirrorCS"),subQ0]}),1.0]])],"derivedFrom":subQ0})])],"isStart":false});}
            var Q18;
            Q18=makeQuery(id+"F11.opExtrude","CAP_EDGE",EDGE,{"disambiguationData":[OSD([sQuery(id+"F10.wireOp",EDGE,"E111.MirrorCS")])],"isStart":false});
            var Q19;
            Q19=makeQuery(id+"F11.opExtrude","CAP_EDGE",EDGE,{"disambiguationData":[OSD([sQuery(id+"F10.wireOp",EDGE,"E113.MirrorCS")])],"isStart":false});
            var Q20;
            Q20=makeQuery(id+"F11.opExtrude","CAP_EDGE",EDGE,{"disambiguationData":[OSD([sQuery(id+"F10.wireOp",EDGE,"E115.MirrorCS")])],"isStart":false});
            var Q21;
            {var subQ0=sQuery(id+"F10.wireOp",EDGE,"E116.MirrorCS");Q21=makeQuery(id+"F11.opExtrude","CAP_EDGE",EDGE,{"disambiguationData":[OSD([subQ0]),TDD([makeQuery(id+"F10.imprint","IMPRINT",EDGE,{"disambiguationData":[TD([[makeQuery(id+"F10.imprint","INTERSECT",VERTEX,{"derivedFrom":[sQuery(id+"F10.wireOp",EDGE,"E110.MirrorCS"),subQ0]}),1.0]])],"derivedFrom":subQ0})])],"isStart":false});}
            fillet(context, id + "F15", {"entities" : qUnion([Q0, Q1, Q2, Q3, Q4, Q5, Q6, Q7, Q8, Q9, Q10, Q11, Q12, Q13, Q14, Q15, Q16, Q17, Q18, Q19, Q20, Q21]), "radius" : .3 * mm, "tangentPropagation" : true, "allowEdgeOverflow" : false});
        }
        {
            var Q0;
            Q0=makeQuery(id+"F1.opExtrude","CAP_FACE",FACE,{"disambiguationData":[OSD([sQuery(id+"F0.wireOp",EDGE,"E0.bottom"),sQuery(id+"F0.wireOp",EDGE,"E0.top"),sQuery(id+"F0.wireOp",EDGE,"E0.left"),sQuery(id+"F0.wireOp",EDGE,"E0.right")])],"isStart":false});
            var sketch = newSketch(context, id + "F16", { "sketchPlane" : qUnion([Q0])});
            skLineSegment(sketch, "E123", {"start": v(0, -7.88) * mm, "end": v(24.5, -7.87) * mm, "construction": true});
            skCircle(sketch, "E124", {"center": v(3, -5.13) * mm, "radius": 1.25 * mm});
            skCircle(sketch, "E125.1.0.0", {"center": v(7, -5.13) * mm, "radius": 1.25 * mm});
            skCircle(sketch, "E125.2.0.0", {"center": v(11, -5.13) * mm, "radius": 1.25 * mm});
            skLineSegment(sketch, "E125.direction1", {"start": v(3, -5.13) * mm, "end": v(7, -5.13) * mm, "construction": true});
            skCircle(sketch, "E126.MirrorC", {"center": v(3, -10.63) * mm, "radius": 1.25 * mm});
            skCircle(sketch, "E127.MirrorC", {"center": v(7, -10.63) * mm, "radius": 1.25 * mm});
            skCircle(sketch, "E128.MirrorC", {"center": v(11, -10.62) * mm, "radius": 1.25 * mm});
            skCircle(sketch, "E129", {"center": v(22, -7.88) * mm, "radius": 1.25 * mm});
            skCircle(sketch, "E130.1.0.0", {"center": v(18, -7.88) * mm, "radius": 1.25 * mm});
            skCircle(sketch, "E130.2.0.0", {"center": v(14, -7.88) * mm, "radius": 1.25 * mm});
            skLineSegment(sketch, "E130.direction1", {"start": v(22, -7.88) * mm, "end": v(18, -7.88) * mm, "construction": true});
            skSolve(sketch);
        }
        {
            var Q0;
            Q0 = qSketchRegion(id + "F16", true);
            var Q1;
            Q1=makeQuery(id+"F1.opExtrude","CAP_FACE",FACE,{"disambiguationData":[OSD([sQuery(id+"F0.wireOp",EDGE,"E0.bottom"),sQuery(id+"F0.wireOp",EDGE,"E0.top"),sQuery(id+"F0.wireOp",EDGE,"E0.left"),sQuery(id+"F0.wireOp",EDGE,"E0.right")])],"isStart":true});
            extrude(context, id + "F17", {"entities" : qUnion([Q0]), "operationType" : NewBodyOperationType.REMOVE, "endBound" : BoundingType.UP_TO_SURFACE, "oppositeDirection" : true, "depth" : 25 * mm, "endBoundEntityFace" : qUnion([Q1]), "offsetDistance" : 25 * mm});
        }
    });
